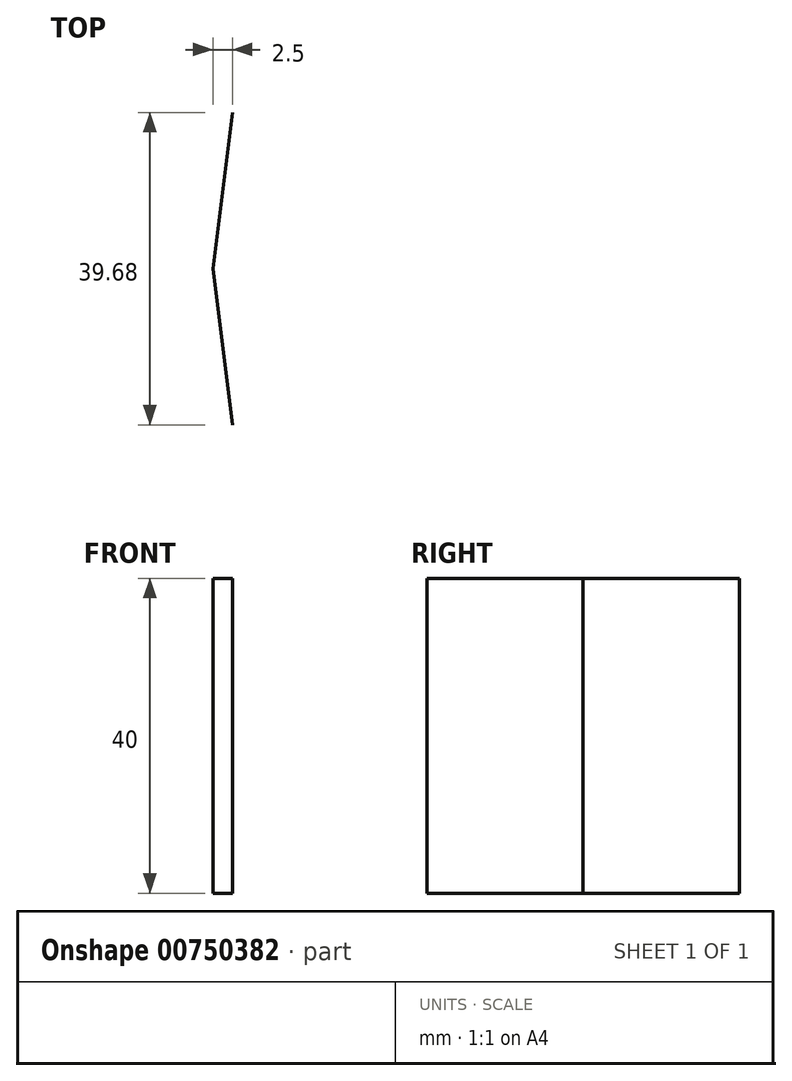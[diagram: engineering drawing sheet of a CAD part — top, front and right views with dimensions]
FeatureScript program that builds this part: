
annotation { "Feature Type Name" : "Feature", "Feature Type Description" : "" }
export const myFeature = defineFeature(function(context is Context, id is Id, definition is map)
    precondition{}
    {
        {
            var Q0;
            Q0=qCreatedBy(makeId("Top.planeOp"),FACE);
            var sketch = newSketch(context, id + "F0", { "sketchPlane" : qUnion([Q0])});
            skLineSegment(sketch, "E0", {"start": v(0, -25.52) * mm, "end": v(0, 25.52) * mm, "construction": true});
            skLineSegment(sketch, "E1", {"start": v(0, 0) * mm, "end": v(80, 0) * mm});
            skLineSegment(sketch, "E2", {"start": v(80, 0) * mm, "end": v(2.5, -19.84) * mm});
            skLineSegment(sketch, "E3", {"start": v(2.5, -19.84) * mm, "end": v(0, 0) * mm});
            skLineSegment(sketch, "E4.MirrorCS", {"start": v(2.5, 19.84) * mm, "end": v(0, 0) * mm});
            skLineSegment(sketch, "E5.MirrorCS", {"start": v(80, 0) * mm, "end": v(2.5, 19.84) * mm});
            skPoint(sketch, "E6", {"position": v(10, 0) * mm});
            skLineSegment(sketch, "E7", {"start": v(0, 0) * mm, "end": v(7.34, -18.6) * mm, "construction": true});
            skLineSegment(sketch, "E8.MirrorCS", {"start": v(0, 0) * mm, "end": v(7.34, 18.6) * mm, "construction": true});
            skSolve(sketch);
        }
        {
            var Q0;
            Q0=qCreatedBy(makeId("Right.planeOp"),FACE);
            var sketch = newSketch(context, id + "F1", { "sketchPlane" : qUnion([Q0])});
            skLineSegment(sketch, "E9", {"start": v(0, 0) * mm, "end": v(0, 40) * mm});
            skSolve(sketch);
        }
        {
            var Q0;
            Q0 = qSketchRegion(id + "F1", true);
            var Q1;
            Q1=sQuery(id+"F0.wireOp",EDGE,"E3");
            var Q2;
            Q2=sQuery(id+"F0.wireOp",EDGE,"E4.MirrorCS");
            var Q3;
            Q3=sQuery(id+"F1.wireOp",VERTEX,"E9.end");
            extrude(context, id + "F2", {"entities" : qUnion([Q0]), "bodyType" : ToolBodyType.SURFACE, "surfaceEntities" : qUnion([Q1, Q2]), "endBound" : BoundingType.UP_TO_VERTEX, "depth" : 25 * mm, "endBoundEntityVertex" : qUnion([Q3]), "offsetDistance" : 25 * mm});
        }
        {
            var Q0;
            Q0=makeQuery(id+"F0.imprint","IMPRINT",FACE,{"disambiguationData":[TD([[makeQuery(id+"F0.imprint","IMPRINT",EDGE,{"derivedFrom":sQuery(id+"F0.wireOp",EDGE,"E1")}),-1.0]])]});
            var Q1;
            Q1=sQuery(id+"F1.wireOp",VERTEX,"E9.end");
            cPlane(context, id + "F3", {"entities" : qUnion([Q0, Q1]), "cplaneType" : CPlaneType.PLANE_POINT, "offset" : 25 * mm, "width" : 150 * mm, "height" : 150 * mm});
        }
        {
            var Q0;
            Q0=qCreatedBy(id+"F3.planeOp",FACE);
            var sketch = newSketch(context, id + "F4", { "sketchPlane" : qUnion([Q0])});
            skLineSegment(sketch, "E10", {"start": v(0, 0) * mm, "end": v(7.34, -18.6) * mm});
            skLineSegment(sketch, "E11", {"start": v(7.34, -18.6) * mm, "end": v(80, 0) * mm});
            skLineSegment(sketch, "E12", {"start": v(80, 0) * mm, "end": v(7.34, 18.6) * mm});
            skLineSegment(sketch, "E13", {"start": v(7.34, 18.6) * mm, "end": v(0, 0) * mm});
            skSolve(sketch);
        }
        {
            var Q0;
            Q0=sQuery(id+"F4.wireOp",VERTEX,"E10.end");
            var Q1;
            Q1=sQuery(id+"F1.wireOp",VERTEX,"E9.end");
            var Q2;
            Q2=sQuery(id+"F0.wireOp",VERTEX,"E3.start");
            cPlane(context, id + "F5", {"entities" : qUnion([Q0, Q1, Q2]), "cplaneType" : CPlaneType.THREE_POINT, "offset" : 25 * mm, "width" : 150 * mm, "height" : 150 * mm});
        }
        {
            var Q0;
            Q0=qCreatedBy(id+"F5.planeOp",FACE);
            var sketch = newSketch(context, id + "F6", { "sketchPlane" : qUnion([Q0])});
            skLineSegment(sketch, "E14", {"start": v(-19.38, 0.33) * mm, "end": v(-18.05, 40.62) * mm});
            skLineSegment(sketch, "E15", {"start": v(-18.05, 40.62) * mm, "end": v(1.93, 39.65) * mm, "construction": true});
            skLineSegment(sketch, "E16", {"start": v(1.93, 39.65) * mm, "end": v(-19.38, 0.33) * mm});
            skLineSegment(sketch, "E17", {"start": v(1.93, 39.65) * mm, "end": v(-17.4, 60.3) * mm});
            skLineSegment(sketch, "E18", {"start": v(-17.4, 60.3) * mm, "end": v(-18.05, 40.62) * mm});
            skSolve(sketch);
        }
        {
            var Q0;
            Q0=qCreatedBy(makeId("Front.planeOp"),FACE);
            var sketch = newSketch(context, id + "F7", { "sketchPlane" : qUnion([Q0])});
            skLineSegment(sketch, "E19", {"start": v(0, 40.06) * mm, "end": v(72.25, 98.84) * mm});
            skSolve(sketch);
        }
        {
            var Q0;
            Q0=sQuery(id+"F6.wireOp",VERTEX,"E17.start");
            var Q1;
            Q1=sQuery(id+"F7.wireOp",VERTEX,"E19.end");
            var Q2;
            Q2=sQuery(id+"F6.wireOp",VERTEX,"E18.start");
            cPlane(context, id + "F8", {"entities" : qUnion([Q0, Q1, Q2]), "cplaneType" : CPlaneType.THREE_POINT, "offset" : 25 * mm, "width" : 150 * mm, "height" : 150 * mm});
        }
    });
